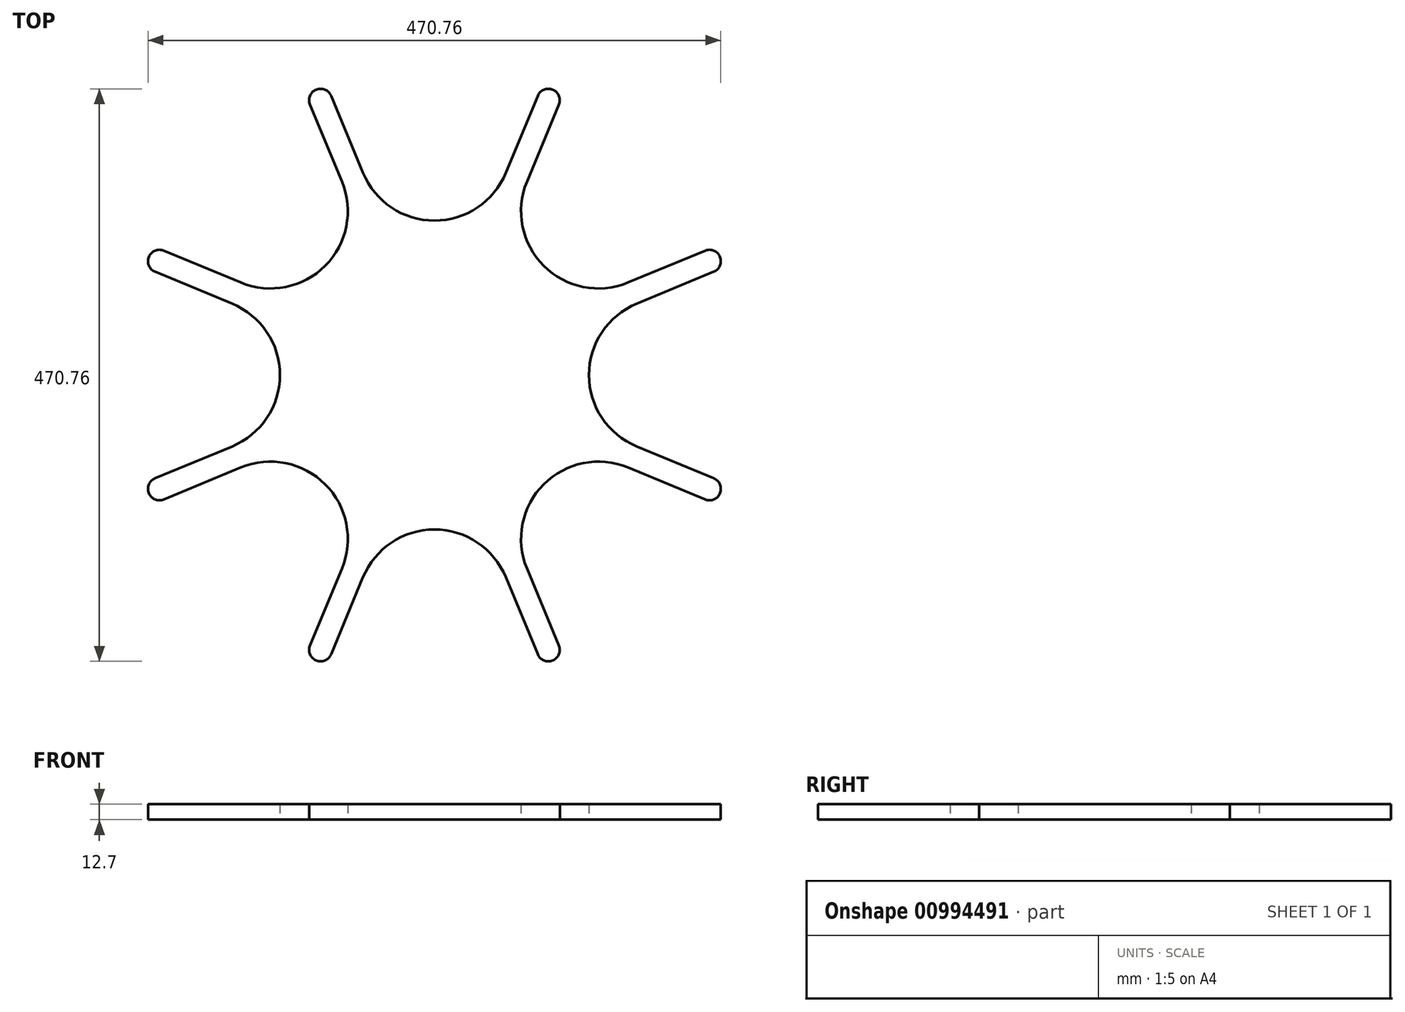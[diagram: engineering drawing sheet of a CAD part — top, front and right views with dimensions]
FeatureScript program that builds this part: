
annotation { "Feature Type Name" : "Feature", "Feature Type Description" : "" }
export const myFeature = defineFeature(function(context is Context, id is Id, definition is map)
    precondition{}
    {
        {
            var Q0;
            Q0=qCreatedBy(makeId("Top.planeOp"),FACE);
            var sketch = newSketch(context, id + "F0", { "sketchPlane" : qUnion([Q0])});
            skArc(sketch, "E0", {"start": v(-238.1, -88.45) * mm, "mid": v(-234.67, -97.2) * mm, "end": v(-230.9, -105.82) * mm});
            skCircle(sketch, "E1", {"center": v(0, 0) * mm, "radius": 190.5 * mm, "construction": true});
            skArc(sketch, "E2", {"start": v(58.67, -166.2) * mm, "mid": v(0, -127) * mm, "end": v(-58.67, -166.2) * mm});
            skLineSegment(sketch, "E3", {"start": v(0, 0) * mm, "end": v(-97.2, -234.67) * mm, "construction": true});
            skLineSegment(sketch, "E4", {"start": v(-58.67, -166.2) * mm, "end": v(-84.92, -229.58) * mm});
            skLineSegment(sketch, "E5", {"start": v(0, 0) * mm, "end": v(0, -254) * mm, "construction": true});
            skLineSegment(sketch, "E6.MirrorCS", {"start": v(58.67, -166.2) * mm, "end": v(88.45, -238.1) * mm});
            skLineSegment(sketch, "E7.1.0", {"start": v(76.04, -159) * mm, "end": v(105.82, -230.9) * mm});
            skArc(sketch, "E7.1.1", {"start": v(159, -76.04) * mm, "mid": v(89.8, -89.8) * mm, "end": v(76.04, -159) * mm});
            skLineSegment(sketch, "E7.1.2", {"start": v(159, -76.04) * mm, "end": v(230.9, -105.82) * mm});
            skLineSegment(sketch, "E7.2.0", {"start": v(166.2, -58.67) * mm, "end": v(238.1, -88.45) * mm});
            skArc(sketch, "E7.2.1", {"start": v(166.2, 58.67) * mm, "mid": v(127, 0) * mm, "end": v(166.2, -58.67) * mm});
            skLineSegment(sketch, "E7.2.2", {"start": v(166.2, 58.67) * mm, "end": v(238.1, 88.45) * mm});
            skLineSegment(sketch, "E7.3.0", {"start": v(159, 76.04) * mm, "end": v(230.9, 105.82) * mm});
            skArc(sketch, "E7.3.1", {"start": v(76.04, 159) * mm, "mid": v(89.8, 89.8) * mm, "end": v(159, 76.04) * mm});
            skLineSegment(sketch, "E7.3.2", {"start": v(76.04, 159) * mm, "end": v(105.82, 230.9) * mm});
            skLineSegment(sketch, "E7.4.0", {"start": v(58.67, 166.2) * mm, "end": v(88.45, 238.1) * mm});
            skArc(sketch, "E7.4.1", {"start": v(-58.67, 166.2) * mm, "mid": v(0, 127) * mm, "end": v(58.67, 166.2) * mm});
            skLineSegment(sketch, "E7.4.2", {"start": v(-58.67, 166.2) * mm, "end": v(-88.45, 238.1) * mm});
            skLineSegment(sketch, "E7.5.0", {"start": v(-76.04, 159) * mm, "end": v(-105.82, 230.9) * mm});
            skArc(sketch, "E7.5.1", {"start": v(-159, 76.04) * mm, "mid": v(-89.8, 89.8) * mm, "end": v(-76.04, 159) * mm});
            skLineSegment(sketch, "E7.5.2", {"start": v(-159, 76.04) * mm, "end": v(-230.9, 105.82) * mm});
            skLineSegment(sketch, "E7.6.0", {"start": v(-166.2, 58.67) * mm, "end": v(-238.1, 88.45) * mm});
            skArc(sketch, "E7.6.1", {"start": v(-166.2, -58.67) * mm, "mid": v(-127, 0) * mm, "end": v(-166.2, 58.67) * mm});
            skLineSegment(sketch, "E7.6.2", {"start": v(-166.2, -58.67) * mm, "end": v(-238.1, -88.45) * mm});
            skLineSegment(sketch, "E7.7.0", {"start": v(-159, -76.04) * mm, "end": v(-230.9, -105.82) * mm});
            skArc(sketch, "E7.7.1", {"start": v(-76.04, -159) * mm, "mid": v(-89.8, -89.8) * mm, "end": v(-159, -76.04) * mm});
            skLineSegment(sketch, "E7.7.2", {"start": v(-76.04, -159) * mm, "end": v(-102.29, -222.38) * mm});
            skLineSegment(sketch, "E8", {"start": v(-58.67, -166.2) * mm, "end": v(-76.04, -159) * mm, "construction": true});
            skPoint(sketch, "E9", {"position": v(-67.35, -162.6) * mm});
            skArc(sketch, "E10.trimOffspring", {"start": v(88.45, -238.1) * mm, "mid": v(97.2, -234.67) * mm, "end": v(105.82, -230.9) * mm});
            skArc(sketch, "E11.trimOffspring", {"start": v(230.9, -105.82) * mm, "mid": v(234.67, -97.2) * mm, "end": v(238.1, -88.45) * mm});
            skArc(sketch, "E12.trimOffspring", {"start": v(238.1, 88.45) * mm, "mid": v(234.67, 97.2) * mm, "end": v(230.9, 105.82) * mm});
            skArc(sketch, "E13.trimOffspring", {"start": v(105.82, 230.9) * mm, "mid": v(97.2, 234.67) * mm, "end": v(88.45, 238.1) * mm});
            skArc(sketch, "E14.trimOffspring", {"start": v(-88.45, 238.1) * mm, "mid": v(-97.2, 234.67) * mm, "end": v(-105.82, 230.9) * mm});
            skArc(sketch, "E15.trimOffspring", {"start": v(-230.9, 105.82) * mm, "mid": v(-234.67, 97.2) * mm, "end": v(-238.1, 88.45) * mm});
            skArc(sketch, "E16", {"start": v(-84.92, -229.58) * mm, "mid": v(-97.2, -234.67) * mm, "end": v(-102.29, -222.38) * mm});
            skPoint(sketch, "E17.orphan", {"position": v(-105.82, -230.9) * mm});
            skPoint(sketch, "E18.orphan", {"position": v(-88.45, -238.1) * mm});
            skArc(sketch, "E19.1.0", {"start": v(102.29, -222.38) * mm, "mid": v(97.2, -234.67) * mm, "end": v(84.92, -229.58) * mm});
            skArc(sketch, "E19.2.0", {"start": v(229.58, -84.92) * mm, "mid": v(234.67, -97.2) * mm, "end": v(222.38, -102.29) * mm});
            skArc(sketch, "E19.3.0", {"start": v(222.38, 102.29) * mm, "mid": v(234.67, 97.2) * mm, "end": v(229.58, 84.92) * mm});
            skArc(sketch, "E19.4.0", {"start": v(84.92, 229.58) * mm, "mid": v(97.2, 234.67) * mm, "end": v(102.29, 222.38) * mm});
            skArc(sketch, "E19.5.0", {"start": v(-102.29, 222.38) * mm, "mid": v(-97.2, 234.67) * mm, "end": v(-84.92, 229.58) * mm});
            skArc(sketch, "E19.6.0", {"start": v(-229.58, 84.92) * mm, "mid": v(-234.67, 97.2) * mm, "end": v(-222.38, 102.29) * mm});
            skArc(sketch, "E19.7.0", {"start": v(-222.38, -102.29) * mm, "mid": v(-234.67, -97.2) * mm, "end": v(-229.58, -84.92) * mm});
            skCircle(sketch, "E20", {"center": v(0, 0) * mm, "radius": 254 * mm});
            skSolve(sketch);
        }
        {
            var Q0;
            Q0=qCreatedBy(makeId("Front.planeOp"),FACE);
            var sketch = newSketch(context, id + "F1", { "sketchPlane" : qUnion([Q0])});
            skLineSegment(sketch, "E21", {"start": v(0, 0) * mm, "end": v(-254, 0) * mm});
            skLineSegment(sketch, "E22", {"start": v(-254, 0) * mm, "end": v(-254, 8.28) * mm});
            skLineSegment(sketch, "E23", {"start": v(-249.85, 14.23) * mm, "end": v(-26.43, 96.87) * mm});
            skLineSegment(sketch, "E24", {"start": v(0, 106.64) * mm, "end": v(0, 101.6) * mm, "construction": true});
            skArc(sketch, "E25", {"start": v(-26.43, 96.87) * mm, "mid": v(-13.43, 100.4) * mm, "end": v(0, 101.6) * mm});
            skLineSegment(sketch, "E26", {"start": v(-26.43, 96.87) * mm, "end": v(0, 106.64) * mm, "construction": true});
            skLineSegment(sketch, "E27", {"start": v(0, 101.6) * mm, "end": v(0, 101.6) * mm});
            skLineSegment(sketch, "E28", {"start": v(0, 101.6) * mm, "end": v(0, 0) * mm});
            skPoint(sketch, "E29.visualSharp", {"position": v(-254, 12.7) * mm});
            skArc(sketch, "E29.filletArc", {"start": v(-249.85, 14.23) * mm, "mid": v(-252.86, 11.9) * mm, "end": v(-254, 8.28) * mm});
            skSolve(sketch);
        }
        {
            var Q0;
            {var subQ22=sQuery(id+"F0.wireOp",EDGE,"E2");Q0=makeQuery(id+"F0.imprint","IMPRINT",FACE,{"disambiguationData":[TD([[makeQuery(id+"F0.imprint","IMPRINT",EDGE,{"derivedFrom":subQ22}),-1.0]])]});}
            extrude(context, id + "F2", {"entities" : qUnion([Q0]), "depth" : 12.7 * mm, "offsetDistance" : 25.4 * mm});
        }
    });
